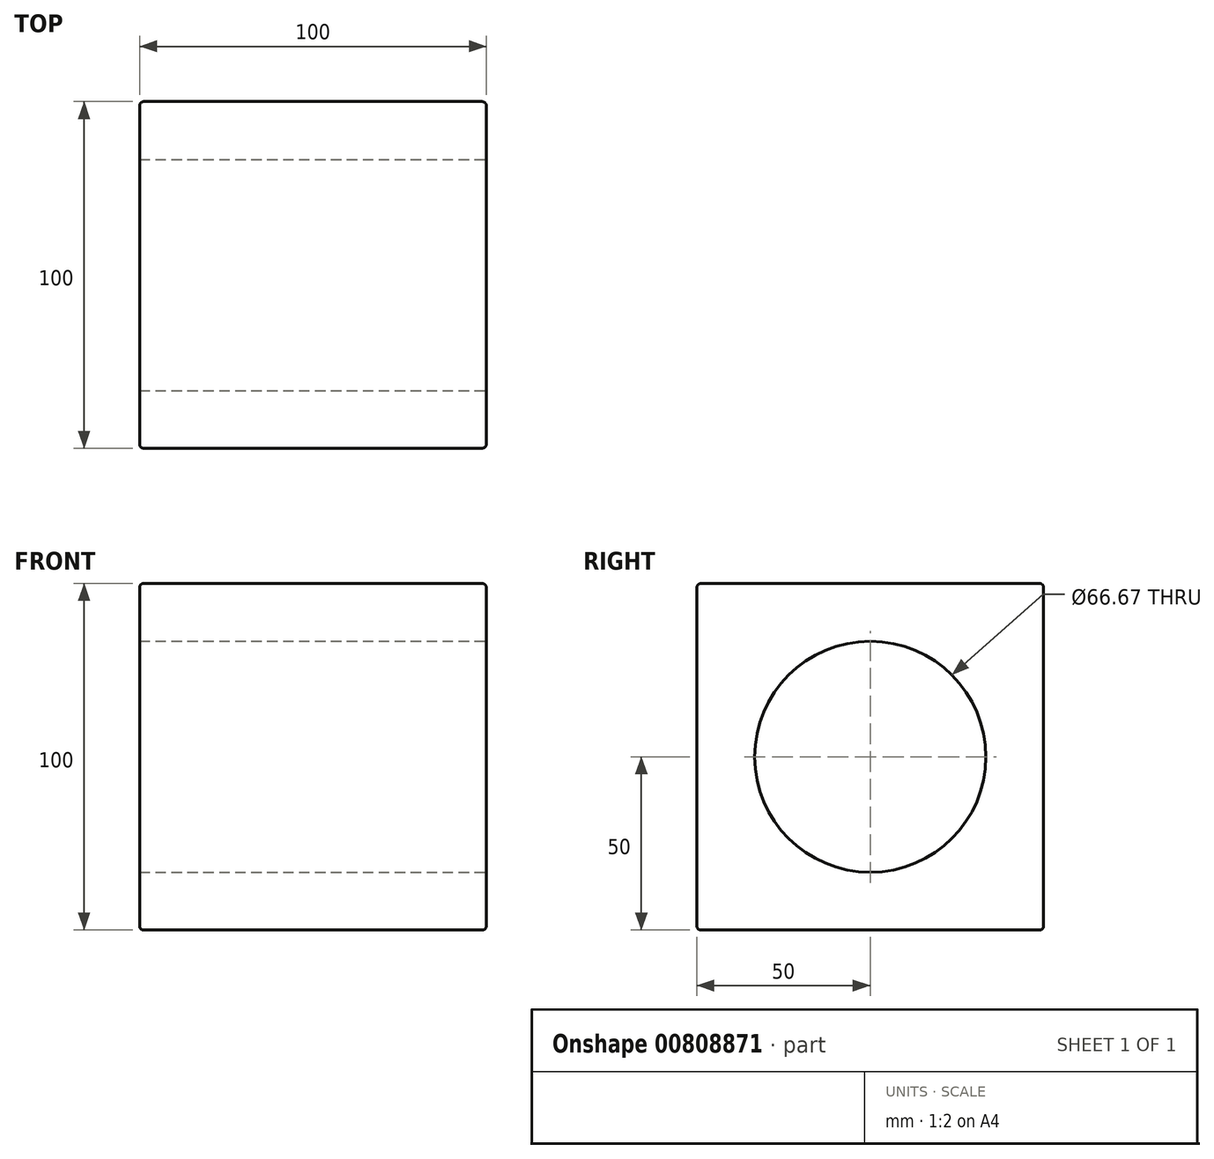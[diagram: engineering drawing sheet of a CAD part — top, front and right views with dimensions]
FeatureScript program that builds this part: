
annotation { "Feature Type Name" : "Feature", "Feature Type Description" : "" }
export const myFeature = defineFeature(function(context is Context, id is Id, definition is map)
    precondition{}
    {
        {
            var Q0;
            Q0=qCreatedBy(makeId("Top.planeOp"),FACE);
            var sketch = newSketch(context, id + "F0", { "sketchPlane" : qUnion([Q0])});
            skLineSegment(sketch, "E0.bottom", {"start": v(50, -50) * mm, "end": v(-50, -50) * mm});
            skLineSegment(sketch, "E0.top", {"start": v(50, 50) * mm, "end": v(-50, 50) * mm});
            skLineSegment(sketch, "E0.left", {"start": v(50, -50) * mm, "end": v(50, 50) * mm});
            skLineSegment(sketch, "E0.right", {"start": v(-50, -50) * mm, "end": v(-50, 50) * mm});
            skPoint(sketch, "E0.middle", {"position": v(0, 0) * mm});
            skSolve(sketch);
        }
        {
            var Q0;
            Q0=qSketchRegion(id+"F0",true);
            extrude(context, id + "F1", {"entities" : qUnion([Q0]), "depth" : 100 * mm, "offsetDistance" : 25 * mm});
        }
        {
            var Q0;
            Q0=makeQuery(id+"F1.opExtrude","CAP_FACE",FACE,{"disambiguationData":[OSD([sQuery(id+"F0.wireOp",EDGE,"E0.bottom"),sQuery(id+"F0.wireOp",EDGE,"E0.top"),sQuery(id+"F0.wireOp",EDGE,"E0.left"),sQuery(id+"F0.wireOp",EDGE,"E0.right")])],"isStart":false});
            var sketch = newSketch(context, id + "F2", { "sketchPlane" : qUnion([Q0])});
            skCircle(sketch, "E1", {"center": v(0, 0) * mm, "radius": 10 * mm});
            skSolve(sketch);
        }
        {
            var Q0;
            Q0=makeQuery(id+"F1.opExtrude","CAP_EDGE",EDGE,{"disambiguationData":[OSD([sQuery(id+"F0.wireOp",EDGE,"E0.right")])],"isStart":false});
            var Q1;
            Q1=makeQuery(id+"F1.opExtrude","CAP_EDGE",EDGE,{"disambiguationData":[OSD([sQuery(id+"F0.wireOp",EDGE,"E0.top")])],"isStart":false});
            var Q2;
            Q2=makeQuery(id+"F1.opExtrude","CAP_EDGE",EDGE,{"disambiguationData":[OSD([sQuery(id+"F0.wireOp",EDGE,"E0.left")])],"isStart":false});
            var Q3;
            Q3=makeQuery(id+"F1.opExtrude","CAP_EDGE",EDGE,{"disambiguationData":[OSD([sQuery(id+"F0.wireOp",EDGE,"E0.bottom")])],"isStart":false});
            var Q4;
            Q4=makeQuery(id+"F1.opExtrude","SWEPT_EDGE",EDGE,{"disambiguationData":[OSD([sQuery(id+"F0.wireOp",EDGE,"E0.bottom"),sQuery(id+"F0.wireOp",EDGE,"E0.right")])]});
            var Q5;
            Q5=makeQuery(id+"F1.opExtrude","SWEPT_EDGE",EDGE,{"disambiguationData":[OSD([sQuery(id+"F0.wireOp",EDGE,"E0.top"),sQuery(id+"F0.wireOp",EDGE,"E0.right")])]});
            var Q6;
            Q6=makeQuery(id+"F1.opExtrude","SWEPT_EDGE",EDGE,{"disambiguationData":[OSD([sQuery(id+"F0.wireOp",EDGE,"E0.bottom"),sQuery(id+"F0.wireOp",EDGE,"E0.left")])]});
            var Q7;
            Q7=makeQuery(id+"F1.opExtrude","SWEPT_EDGE",EDGE,{"disambiguationData":[OSD([sQuery(id+"F0.wireOp",EDGE,"E0.top"),sQuery(id+"F0.wireOp",EDGE,"E0.left")])]});
            var Q8;
            Q8=makeQuery(id+"F1.opExtrude","CAP_EDGE",EDGE,{"disambiguationData":[OSD([sQuery(id+"F0.wireOp",EDGE,"E0.left")])],"isStart":true});
            var Q9;
            Q9=makeQuery(id+"F1.opExtrude","CAP_EDGE",EDGE,{"disambiguationData":[OSD([sQuery(id+"F0.wireOp",EDGE,"E0.bottom")])],"isStart":true});
            var Q10;
            Q10=makeQuery(id+"F1.opExtrude","CAP_EDGE",EDGE,{"disambiguationData":[OSD([sQuery(id+"F0.wireOp",EDGE,"E0.right")])],"isStart":true});
            var Q11;
            Q11=makeQuery(id+"F1.opExtrude","CAP_EDGE",EDGE,{"disambiguationData":[OSD([sQuery(id+"F0.wireOp",EDGE,"E0.top")])],"isStart":true});
            fillet(context, id + "F3", {"entities" : qUnion([Q0, Q1, Q2, Q3, Q4, Q5, Q6, Q7, Q8, Q9, Q10, Q11]), "radius" : 1.2 * mm, "tangentPropagation" : true, "allowEdgeOverflow" : false});
        }
        {
            var Q0;
            Q0=makeQuery(id+"F1.opExtrude","SWEPT_FACE",FACE,{"disambiguationData":[OSD([sQuery(id+"F0.wireOp",EDGE,"E0.left")])]});
            var sketch = newSketch(context, id + "F4", { "sketchPlane" : qUnion([Q0])});
            skCircle(sketch, "E2", {"center": v(0, 50) * mm, "radius": 33.33 * mm});
            skSolve(sketch);
        }
        {
            var Q0;
            Q0=makeQuery(id+"F4.imprint","IMPRINT",FACE,{"disambiguationData":[TD([[makeQuery(id+"F4.imprint","IMPRINT",EDGE,{"derivedFrom":sQuery(id+"F4.wireOp",EDGE,"E2")}),1.0]])]});
            extrude(context, id + "F5", {"entities" : qUnion([Q0]), "operationType" : NewBodyOperationType.REMOVE, "endBound" : BoundingType.THROUGH_ALL, "oppositeDirection" : true, "depth" : 25 * mm, "offsetDistance" : 25 * mm});
        }
    });
